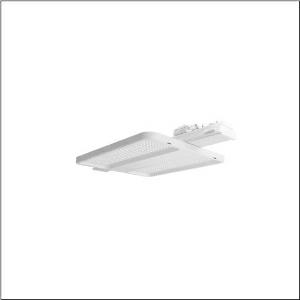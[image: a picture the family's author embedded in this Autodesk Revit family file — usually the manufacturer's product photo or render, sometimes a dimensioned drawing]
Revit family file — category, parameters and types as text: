
# Revit family: highbay_11_fur_licross_r__tragschiene_midi_51hn12da5fla_24f2
name_source: partatom
category: Lighting Fixtures
units: mm (PartAtom-declared; Revit-internal decimal feet)

## family parameters
Cut with Voids When Loaded = No
Host = Face
Light Source = No
Part Type = Normal
Room Calculation Point = No
Round Connector Dimension = Use Diameter
Shared = No

## types (1)
- --- (1 x LED, 14930 lm, 73.2 W, 5000K)
    Apparent Load = 73 VA
    CIE Flux Codes = 87 98 100 100 100
    Color Rendering = 80
    Color Temperature = 5000K
    Default Elevation = 1800 mm
    Description = high bay luminaire Highbay 11 for Licross® trunking rail midi; direct symmetric wide distribution, light control with lens of PMMA; UGR ≤ 22 (X = 4H | Y = 8H | S = 0.25H | reflection values 70/50/20); luminous flux: 14.930lm; light colour: 850, colour temperature: 5000K, MacAdam ≤ 2 SDCM (initial), colour rendering: CRI > 80; luminous efficacy: 204lm/W; rated service life: 100.000h (L95/B50) at AT= 25°C; control: DALI 2; luminaire connection: plug, 5-pole, with phase selectionmains connection: 230..240V, AC 50/60Hz; connected load: 73,2W; protection rating (complete): IP64; insulation class (complete): insulation class I (protective earthing); protection symbol: D; impact resistance: IK07; certification: CE, ENEC, VDE, UKCA; internal wiring halogen-free; luminaire LABS conformity tested according to VDMA 24364:2018-05; corresponds to IFS (International Featured Standards) requirements for safety and quality in the food industry; housing frame of high-performance plastic PA6, matt traffic white (RAL 9016); cover of PMMA; fixing on rail side of steel, galvanised, white; blank cover of PC/ABS, traffic white (RAL 9016); dimension (LxWxH): 750 x 442 x 71mm; permissible operating ambient temperature: -40..+55°C (reducing of maximum allowable ambient temperature of 5°C with ceiling mounting); packaging unit: 1 piece
    Height = 72 mm  [stored 0.23622 ft]
    Lamp = 1 x LED
    Lamp Light Flux = 14930 lm
    Lamp Power = 73.2 W
    Lamp count = 1
    Length = 474 mm
    Luminous efficacy = 204 lm/W
    Manufacturer = Siteco
    ModVariant = No
    Model = 51HN12DA5FLA
    Mounting Place = Ceiling
    Mounting Type = Pendant
    Number of Poles = 1
    OnlyDefault = Yes
    Power Factor = 1
    Product Name = Highbay 11 für Licross® Tragschiene midi
    Product group = high bay luminaire
    ProductGroupID = 901
    Protection Class = Protection class I
    Protection Degree = IP 64
    RLX_Detail_Level = 1
    RLX_Emergency_Light_Flux = 0 lm
    RLX_Emergency_Type = 0
    RLX_Emergency_Type_DB = No
    RlxData = <blob elided: 17041 chars, md5=e46f21b9>
    Socket = socket
    Standby Power = 0 W
    System Light Flux = 14930 lm
    System Power = 73 W
    Type Comments = factory setting: luminous flux: 100 % | dim-lin: 254 | 339 mA
    Type Image = l_1363258.jpg
    URL = http://relux.com
    VarID = @adj_007473
    Voltage = 0 V
    Weight = 0.00 kg
    Width = 442 mm

note: [stored X ft] marks values corroborated as IEEE doubles in the binary element streams (Revit-internal decimal feet)

## geometry (parser evidence)
native form markers: Blend x4, Sweep x9
no freeform markers — native parametric forms only
